# Revit family: HARMANN - REVIT - MAXEE - poziomy
name_source: partatom
category: Wyposażenie mechaniczne
units: mm (PartAtom-declared; Revit-internal decimal feet)

## family parameters
Klasyfikacja = Brak
Obiekt nadrzędny = Powierzchnia
Punkt obliczania pomieszczeń = Nie
Tnij formami wycięć po wczytaniu = Nie
Typ części = Normalny
Współdzielony = Nie
Wymiar okrągłego złącza = Użyj średnicy
Zachowaj orientację opisów = Nie

## types (40) — shared parameters
Autor = https://www.archispace.com
Domyślna rzędna = 1219.2 mm
Opis = Kanałowy wentylator bytowy
Producent = Harmann Polska Sp. z o.o.
Temperatura pracy T = 60 °C
Zasilanie Częstotliwość Minimalna fmin = 20 Hz
Zasilanie Częstotliwość Nominalna fnom = 50 Hz
Zasilanie Ilość faz = 3
Zasilanie napięcie nominalne Unom = 400 V

## per-type parameters (varying)
- MAXEE 1250/6/119600T: A=1370 mm; Akc ESD=HARMANN - Akcesoria - ESD : ESD 1250; Akc EXP=HARMANN - Akcesoria - EXP : EXP 1250; Akc FAL=HARMANN - Akcesoria - FAL : FAL 1250; Akc FSD=HARMANN - Akcesoria - FSD : FSD 11; Akc RAF=HARMANN - Akcesoria - RAF : RAF 1250; Akc RVK H=HARMANN - Akcesoria - RVK H : RVK H 1250; Akc RVS=HARMANN - Akcesoria - RVS : RVS 1250; Akc SGE=HARMANN - Akcesoria - SGE : SGE 1250; Akc SGE dla ESD=HARMANN - Akcesoria - SGE : SGE 1400; B=728 mm; C=1320 mm; Ciśnienie akustyczne nominalne obudowa Lpa=89 dB(A); D=1250 mm; D2=1256 mm; Długość MAXEE=728 mm; F=997 mm; Klasa odporności ogniowej Tmax=brak; Lookup Table Name=MAXEE; MAXEE=HARMANN - MAXEE : MAXEE 1250/6/119600T; Masa=550.00 kg; Moc akustyczna nominalna obudowa Lwa=96 dB(A); Model=MAXEE 1250/6/119600T; N1=40  [stored 0.131234 ft]; Numer artykułu=16259200; Obroty nominalne nnom=1190.000 obr./min; Powietrze Przepływ Maksymalny Qmax=119640.0 m³/h; Powietrze ciśnienie statyczne maksymalne dPmax=1015.0 Pa; R2=625 mm; Wysokość=498 mm; Wysokość FAL=270 mm; Wysokość FSD=94 mm; Zasilanie Częstotliwość Maksymalna fmax=60 Hz; Zasilanie Moc maksymalna Pmax=37683 W; Zasilanie natężenie maksymalne Imax=69 A
- MAXEE 1250/6/109300T: A=1370 mm; Akc ESD=HARMANN - Akcesoria - ESD : ESD 1250; Akc EXP=HARMANN - Akcesoria - EXP : EXP 1250; Akc FAL=HARMANN - Akcesoria - FAL : FAL 1250; Akc FSD=HARMANN - Akcesoria - FSD : FSD 11; Akc RAF=HARMANN - Akcesoria - RAF : RAF 1250; Akc RVK H=HARMANN - Akcesoria - RVK H : RVK H 1250; Akc RVS=HARMANN - Akcesoria - RVS : RVS 1250; Akc SGE=HARMANN - Akcesoria - SGE : SGE 1250; Akc SGE dla ESD=HARMANN - Akcesoria - SGE : SGE 1250; B=728 mm; C=1320 mm; Ciśnienie akustyczne nominalne obudowa Lpa=88 dB(A); D=1250 mm; D2=1256 mm; Długość MAXEE=728 mm; F=997 mm; Klasa odporności ogniowej Tmax=brak; Lookup Table Name=MAXEE; MAXEE=HARMANN - MAXEE : MAXEE 1250/6/109300T; Masa=376.00 kg; Moc akustyczna nominalna obudowa Lwa=95 dB(A); Model=MAXEE 1250/6/109300T; N1=39  [stored 0.127953 ft]; Numer artykułu=16258300; Obroty nominalne nnom=1080.000 obr./min; Powietrze Przepływ Maksymalny Qmax=109260.0 m³/h; Powietrze ciśnienie statyczne maksymalne dPmax=835.0 Pa; R2=625 mm; Wysokość=498 mm; Wysokość FAL=270 mm; Wysokość FSD=94 mm; Zasilanie Częstotliwość Maksymalna fmax=55 Hz; Zasilanie Moc maksymalna Pmax=28129 W; Zasilanie natężenie maksymalne Imax=52 A
- MAXEE 1250/6/98500T: A=1370 mm; Akc ESD=HARMANN - Akcesoria - ESD : ESD 1250; Akc EXP=HARMANN - Akcesoria - EXP : EXP 1250; Akc FAL=HARMANN - Akcesoria - FAL : FAL 1250; Akc FSD=HARMANN - Akcesoria - FSD : FSD 11; Akc RAF=HARMANN - Akcesoria - RAF : RAF 1250; Akc RVK H=HARMANN - Akcesoria - RVK H : RVK H 1250; Akc RVS=HARMANN - Akcesoria - RVS : RVS 1250; Akc SGE=HARMANN - Akcesoria - SGE : SGE 1250; Akc SGE dla ESD=HARMANN - Akcesoria - SGE : SGE 1400; B=728 mm; C=1320 mm; Ciśnienie akustyczne nominalne obudowa Lpa=89 dB(A); D=1250 mm; D2=1256 mm; Długość MAXEE=728 mm; F=997 mm; Klasa odporności ogniowej Tmax=brak; Lookup Table Name=MAXEE; MAXEE=HARMANN - MAXEE : MAXEE 1250/6/98500T; Masa=365.00 kg; Moc akustyczna nominalna obudowa Lwa=96 dB(A); Model=MAXEE 1250/6/98500T; N1=38  [stored 0.124672 ft]; Numer artykułu=16257900; Obroty nominalne nnom=990.000 obr./min; Powietrze Przepływ Maksymalny Qmax=98520.0 m³/h; Powietrze ciśnienie statyczne maksymalne dPmax=670.0 Pa; R2=625 mm; Wysokość=498 mm; Wysokość FAL=270 mm; Wysokość FSD=94 mm; Zasilanie Częstotliwość Maksymalna fmax=50 Hz; Zasilanie Moc maksymalna Pmax=21529 W; Zasilanie natężenie maksymalne Imax=41 A
- MAXEE 1250/6/79400T: A=1370 mm; Akc ESD=HARMANN - Akcesoria - ESD : ESD 1250; Akc EXP=HARMANN - Akcesoria - EXP : EXP 1250; Akc FAL=HARMANN - Akcesoria - FAL : FAL 1250; Akc FSD=HARMANN - Akcesoria - FSD : FSD 11; Akc RAF=HARMANN - Akcesoria - RAF : RAF 1250; Akc RVK H=HARMANN - Akcesoria - RVK H : RVK H 1250; Akc RVS=HARMANN - Akcesoria - RVS : RVS 1250; Akc SGE=HARMANN - Akcesoria - SGE : SGE 1250; Akc SGE dla ESD=HARMANN - Akcesoria - SGE : SGE 1400; B=728 mm; C=1320 mm; Ciśnienie akustyczne nominalne obudowa Lpa=80 dB(A); D=1250 mm; D2=1256 mm; Długość MAXEE=728 mm; F=874 mm; Klasa odporności ogniowej Tmax=400 [oC/2h]; Lookup Table Name=MAXEE; MAXEE=HARMANN - MAXEE : MAXEE 1250/6/79400T; Masa=280.00 kg; Moc akustyczna nominalna obudowa Lwa=87 dB(A); Model=MAXEE 1250/6/79400T; N1=37  [stored 0.121391 ft]; Numer artykułu=16257300; Obroty nominalne nnom=780.000 obr./min; Powietrze Przepływ Maksymalny Qmax=79450.0 m³/h; Powietrze ciśnienie statyczne maksymalne dPmax=420.0 Pa; R2=625 mm; Wysokość=498 mm; Wysokość FAL=270 mm; Wysokość FSD=94 mm; Zasilanie Częstotliwość Maksymalna fmax=40 Hz; Zasilanie Moc maksymalna Pmax=10850 W; Zasilanie natężenie maksymalne Imax=26 A
- MAXEE 1120/6/85800T: A=1240 mm; Akc ESD=HARMANN - Akcesoria - ESD : ESD 1120; Akc EXP=HARMANN - Akcesoria - EXP : EXP 1120; Akc FAL=HARMANN - Akcesoria - FAL : FAL 1120; Akc FSD=HARMANN - Akcesoria - FSD : FSD 11; Akc RAF=HARMANN - Akcesoria - RAF : RAF 1120; Akc RVK H=HARMANN - Akcesoria - RVK H : RVK H 1120; Akc RVS=HARMANN - Akcesoria - RVS : RVS 1120; Akc SGE=HARMANN - Akcesoria - SGE : SGE 1120; Akc SGE dla ESD=HARMANN - Akcesoria - SGE : SGE 1250; B=728 mm; C=1190 mm; Ciśnienie akustyczne nominalne obudowa Lpa=87 dB(A); D=1120 mm; D2=1126 mm; Długość MAXEE=728 mm; F=967 mm; Klasa odporności ogniowej Tmax=brak; Lookup Table Name=MAXEE; MAXEE=HARMANN - MAXEE : MAXEE 1120/6/85800T; Masa=345.00 kg; Moc akustyczna nominalna obudowa Lwa=94 dB(A); Model=MAXEE 1120/6/85800T; N1=36  [stored 0.11811 ft]; Numer artykułu=16271100; Obroty nominalne nnom=1190.000 obr./min; Powietrze Przepływ Maksymalny Qmax=85820.0 m³/h; Powietrze ciśnienie statyczne maksymalne dPmax=765.0 Pa; R2=560 mm; Wysokość=433 mm; Wysokość FAL=270 mm; Wysokość FSD=94 mm; Zasilanie Częstotliwość Maksymalna fmax=60 Hz; Zasilanie Moc maksymalna Pmax=20147 W; Zasilanie natężenie maksymalne Imax=38 A
- MAXEE 1120/6/71400T: A=1240 mm; Akc ESD=HARMANN - Akcesoria - ESD : ESD 1120; Akc EXP=HARMANN - Akcesoria - EXP : EXP 1120; Akc FAL=HARMANN - Akcesoria - FAL : FAL 1120; Akc FSD=HARMANN - Akcesoria - FSD : FSD 11; Akc RAF=HARMANN - Akcesoria - RAF : RAF 1120; Akc RVK H=HARMANN - Akcesoria - RVK H : RVK H 1120; Akc RVS=HARMANN - Akcesoria - RVS : RVS 1120; Akc SGE=HARMANN - Akcesoria - SGE : SGE 1120; Akc SGE dla ESD=HARMANN - Akcesoria - SGE : SGE 1250; B=728 mm; C=1190 mm; Ciśnienie akustyczne nominalne obudowa Lpa=86 dB(A); D=1120 mm; D2=1126 mm; Długość MAXEE=728 mm; F=844 mm; Klasa odporności ogniowej Tmax=brak; Lookup Table Name=MAXEE; MAXEE=HARMANN - MAXEE : MAXEE 1120/6/71400T; Masa=298.00 kg; Moc akustyczna nominalna obudowa Lwa=93 dB(A); Model=MAXEE 1120/6/71400T; N1=35  [stored 0.114829 ft]; Numer artykułu=16270700; Obroty nominalne nnom=990.000 obr./min; Powietrze Przepływ Maksymalny Qmax=71380.0 m³/h; Powietrze ciśnienie statyczne maksymalne dPmax=545.0 Pa; R2=560 mm; Wysokość=433 mm; Wysokość FAL=270 mm; Wysokość FSD=94 mm; Zasilanie Częstotliwość Maksymalna fmax=50 Hz; Zasilanie Moc maksymalna Pmax=12903 W; Zasilanie natężenie maksymalne Imax=24 A
- MAXEE 1120/6/62200T: A=1240 mm; Akc ESD=HARMANN - Akcesoria - ESD : ESD 1120; Akc EXP=HARMANN - Akcesoria - EXP : EXP 1120; Akc FAL=HARMANN - Akcesoria - FAL : FAL 1120; Akc FSD=HARMANN - Akcesoria - FSD : FSD 11; Akc RAF=HARMANN - Akcesoria - RAF : RAF 1120; Akc RVK H=HARMANN - Akcesoria - RVK H : RVK H 1120; Akc RVS=HARMANN - Akcesoria - RVS : RVS 1120; Akc SGE=HARMANN - Akcesoria - SGE : SGE 1120; Akc SGE dla ESD=HARMANN - Akcesoria - SGE : SGE 1250; B=728 mm; C=1190 mm; Ciśnienie akustyczne nominalne obudowa Lpa=80 dB(A); D=1120 mm; D2=1126 mm; Długość MAXEE=728 mm; F=745 mm; Klasa odporności ogniowej Tmax=brak; Lookup Table Name=MAXEE; MAXEE=HARMANN - MAXEE : MAXEE 1120/6/62200T; Masa=218.00 kg; Moc akustyczna nominalna obudowa Lwa=87 dB(A); Model=MAXEE 1120/6/62200T; N1=34  [stored 0.111549 ft]; Numer artykułu=16271500; Obroty nominalne nnom=860.000 obr./min; Powietrze Przepływ Maksymalny Qmax=62250.0 m³/h; Powietrze ciśnienie statyczne maksymalne dPmax=390.0 Pa; R2=560 mm; Wysokość=433 mm; Wysokość FAL=270 mm; Wysokość FSD=94 mm; Zasilanie Częstotliwość Maksymalna fmax=45 Hz; Zasilanie Moc maksymalna Pmax=7053 W; Zasilanie natężenie maksymalne Imax=16 A
- MAXEE 1000/4/76100T: A=1110 mm; Akc ESD=HARMANN - Akcesoria - ESD : ESD 1000; Akc EXP=HARMANN - Akcesoria - EXP : EXP 1000; Akc FAL=HARMANN - Akcesoria - FAL : FAL 1000; Akc FSD=HARMANN - Akcesoria - FSD : FSD 11; Akc RAF=HARMANN - Akcesoria - RAF : RAF 1000; Akc RVK H=HARMANN - Akcesoria - RVK H : RVK H 1000; Akc RVS=HARMANN - Akcesoria - RVS : RVS 1000; Akc SGE=HARMANN - Akcesoria - SGE : SGE 1000; Akc SGE dla ESD=HARMANN - Akcesoria - SGE : SGE 1120; B=638 mm; C=1070 mm; Ciśnienie akustyczne nominalne obudowa Lpa=87 dB(A); D=1000 mm; D2=1006 mm; Długość MAXEE=638 mm; F=834 mm; Klasa odporności ogniowej Tmax=brak; Lookup Table Name=MAXEE; MAXEE=HARMANN - MAXEE : MAXEE 1000/4/76100T; Masa=280.00 kg; Moc akustyczna nominalna obudowa Lwa=94 dB(A); Model=MAXEE 1000/4/76100T; N1=33  [stored 0.108268 ft]; Numer artykułu=16264100; Obroty nominalne nnom=1480.000 obr./min; Powietrze Przepływ Maksymalny Qmax=76095.0 m³/h; Powietrze ciśnienie statyczne maksymalne dPmax=970.0 Pa; R2=500 mm; Wysokość=383 mm; Wysokość FAL=250 mm; Wysokość FSD=94 mm; Zasilanie Częstotliwość Maksymalna fmax=50 Hz; Zasilanie Moc maksymalna Pmax=23206 W; Zasilanie natężenie maksymalne Imax=41 A
- MAXEE 1000/4/75800T: A=1110 mm; Akc ESD=HARMANN - Akcesoria - ESD : ESD 1000; Akc EXP=HARMANN - Akcesoria - EXP : EXP 1000; Akc FAL=HARMANN - Akcesoria - FAL : FAL 1000; Akc FSD=HARMANN - Akcesoria - FSD : FSD 11; Akc RAF=HARMANN - Akcesoria - RAF : RAF 1000; Akc RVK H=HARMANN - Akcesoria - RVK H : RVK H 1000; Akc RVS=HARMANN - Akcesoria - RVS : RVS 1000; Akc SGE=HARMANN - Akcesoria - SGE : SGE 1000; Akc SGE dla ESD=HARMANN - Akcesoria - SGE : SGE 1120; B=638 mm; C=1070 mm; Ciśnienie akustyczne nominalne obudowa Lpa=84 dB(A); D=1000 mm; D2=1006 mm; Długość MAXEE=638 mm; F=872 mm; Klasa odporności ogniowej Tmax=brak; Lookup Table Name=MAXEE_HT; MAXEE=HARMANN - MAXEE : MAXEE 1000/4/75800T; Masa=313.00 kg; Moc akustyczna nominalna obudowa Lwa=91 dB(A); Model=MAXEE 1000/4/75800T; N1=32  [stored 0.104987 ft]; Numer artykułu=16264800; Obroty nominalne nnom=1480.000 obr./min; Powietrze Przepływ Maksymalny Qmax=75810.0 m³/h; Powietrze ciśnienie statyczne maksymalne dPmax=980.0 Pa; R2=500 mm; Wysokość=383 mm; Wysokość FAL=250 mm; Wysokość FSD=94 mm; Zasilanie Częstotliwość Maksymalna fmax=50 Hz; Zasilanie Moc maksymalna Pmax=22034 W; Zasilanie natężenie maksymalne Imax=41 A
- MAXEE 1000/4/67500T: A=1110 mm; Akc ESD=HARMANN - Akcesoria - ESD : ESD 1000; Akc EXP=HARMANN - Akcesoria - EXP : EXP 1000; Akc FAL=HARMANN - Akcesoria - FAL : FAL 1000; Akc FSD=HARMANN - Akcesoria - FSD : FSD 11; Akc RAF=HARMANN - Akcesoria - RAF : RAF 1000; Akc RVK H=HARMANN - Akcesoria - RVK H : RVK H 1000; Akc RVS=HARMANN - Akcesoria - RVS : RVS 1000; Akc SGE=HARMANN - Akcesoria - SGE : SGE 1000; Akc SGE dla ESD=HARMANN - Akcesoria - SGE : SGE 1120; B=638 mm; C=1070 mm; Ciśnienie akustyczne nominalne obudowa Lpa=82 dB(A); D=1000 mm; D2=1006 mm; Długość MAXEE=638 mm; F=814 mm; Klasa odporności ogniowej Tmax=brak; Lookup Table Name=MAXEE; MAXEE=HARMANN - MAXEE : MAXEE 1000/4/67500T; Masa=264.00 kg; Moc akustyczna nominalna obudowa Lwa=89 dB(A); Model=MAXEE 1000/4/67500T; N1=31  [stored 0.101706 ft]; Numer artykułu=16263600; Obroty nominalne nnom=1330.000 obr./min; Powietrze Przepływ Maksymalny Qmax=67550.0 m³/h; Powietrze ciśnienie statyczne maksymalne dPmax=1160.0 Pa; R2=500 mm; Wysokość=383 mm; Wysokość FAL=250 mm; Wysokość FSD=94 mm; Zasilanie Częstotliwość Maksymalna fmax=45 Hz; Zasilanie Moc maksymalna Pmax=16042 W; Zasilanie natężenie maksymalne Imax=33 A
- MAXEE 1000/6/60100T: A=1110 mm; Akc ESD=HARMANN - Akcesoria - ESD : ESD 1000; Akc EXP=HARMANN - Akcesoria - EXP : EXP 1000; Akc FAL=HARMANN - Akcesoria - FAL : FAL 1000; Akc FSD=HARMANN - Akcesoria - FSD : FSD 11; Akc RAF=HARMANN - Akcesoria - RAF : RAF 1000; Akc RVK H=HARMANN - Akcesoria - RVK H : RVK H 1000; Akc RVS=HARMANN - Akcesoria - RVS : RVS 1000; Akc SGE=HARMANN - Akcesoria - SGE : SGE 1000; Akc SGE dla ESD=HARMANN - Akcesoria - SGE : SGE 1120; B=638 mm; C=1070 mm; Ciśnienie akustyczne nominalne obudowa Lpa=78 dB(A); D=1000 mm; D2=1006 mm; Długość MAXEE=638 mm; F=814 mm; Klasa odporności ogniowej Tmax=brak; Lookup Table Name=MAXEE; MAXEE=HARMANN - MAXEE : MAXEE 1000/6/60100T; Masa=265.00 kg; Moc akustyczna nominalna obudowa Lwa=85 dB(A); Model=MAXEE 1000/6/60100T; N1=30  [stored 0.0984252 ft]; Numer artykułu=16263100; Obroty nominalne nnom=1185.000 obr./min; Powietrze Przepływ Maksymalny Qmax=60140.0 m³/h; Powietrze ciśnienie statyczne maksymalne dPmax=610.0 Pa; R2=500 mm; Wysokość=383 mm; Wysokość FAL=250 mm; Wysokość FSD=94 mm; Zasilanie Częstotliwość Maksymalna fmax=60 Hz; Zasilanie Moc maksymalna Pmax=15647 W; Zasilanie natężenie maksymalne Imax=22 A
- MAXEE 1000/4/60000T: A=1110 mm; Akc ESD=HARMANN - Akcesoria - ESD : ESD 1000; Akc EXP=HARMANN - Akcesoria - EXP : EXP 1000; Akc FAL=HARMANN - Akcesoria - FAL : FAL 1000; Akc FSD=HARMANN - Akcesoria - FSD : FSD 11; Akc RAF=HARMANN - Akcesoria - RAF : RAF 1000; Akc RVK H=HARMANN - Akcesoria - RVK H : RVK H 1000; Akc RVS=HARMANN - Akcesoria - RVS : RVS 1000; Akc SGE=HARMANN - Akcesoria - SGE : SGE 1000; Akc SGE dla ESD=HARMANN - Akcesoria - SGE : SGE 1120; B=638 mm; C=1070 mm; Ciśnienie akustyczne nominalne obudowa Lpa=78 dB(A); D=1000 mm; D2=1006 mm; Długość MAXEE=638 mm; F=770 mm; Klasa odporności ogniowej Tmax=brak; Lookup Table Name=MAXEE; MAXEE=HARMANN - MAXEE : MAXEE 1000/4/60000T; Masa=220.00 kg; Moc akustyczna nominalna obudowa Lwa=85 dB(A); Model=MAXEE 1000/4/60000T; N1=29  [stored 0.0951444 ft]; Numer artykułu=16261800; Obroty nominalne nnom=1185.000 obr./min; Powietrze Przepływ Maksymalny Qmax=60040.0 m³/h; Powietrze ciśnienie statyczne maksymalne dPmax=600.0 Pa; R2=500 mm; Wysokość=383 mm; Wysokość FAL=250 mm; Wysokość FSD=94 mm; Zasilanie Częstotliwość Maksymalna fmax=40 Hz; Zasilanie Moc maksymalna Pmax=11300 W; Zasilanie natężenie maksymalne Imax=27 A
- MAXEE 1000/6/49300T: A=1110 mm; Akc ESD=HARMANN - Akcesoria - ESD : ESD 1000; Akc EXP=HARMANN - Akcesoria - EXP : EXP 1000; Akc FAL=HARMANN - Akcesoria - FAL : FAL 1000; Akc FSD=HARMANN - Akcesoria - FSD : FSD 11; Akc RAF=HARMANN - Akcesoria - RAF : RAF 1000; Akc RVK H=HARMANN - Akcesoria - RVK H : RVK H 1000; Akc RVS=HARMANN - Akcesoria - RVS : RVS 1000; Akc SGE=HARMANN - Akcesoria - SGE : SGE 1000; Akc SGE dla ESD=HARMANN - Akcesoria - SGE : SGE 1120; B=638 mm; C=1070 mm; Ciśnienie akustyczne nominalne obudowa Lpa=78 dB(A); D=1000 mm; D2=1006 mm; Długość MAXEE=638 mm; F=715 mm; Klasa odporności ogniowej Tmax=brak; Lookup Table Name=MAXEE_HT; MAXEE=HARMANN - MAXEE : MAXEE 1000/6/49300T; Masa=195.00 kg; Moc akustyczna nominalna obudowa Lwa=85 dB(A); Model=MAXEE 1000/6/49300T; N1=28  [stored 0.0918635 ft]; Numer artykułu=16265200; Obroty nominalne nnom=980.000 obr./min; Powietrze Przepływ Maksymalny Qmax=49290.0 m³/h; Powietrze ciśnienie statyczne maksymalne dPmax=400.0 Pa; R2=500 mm; Wysokość=383 mm; Wysokość FAL=250 mm; Wysokość FSD=94 mm; Zasilanie Częstotliwość Maksymalna fmax=50 Hz; Zasilanie Moc maksymalna Pmax=6663 W; Zasilanie natężenie maksymalne Imax=14 A
- MAXEE 900/4/60300T: A=1010 mm; Akc ESD=HARMANN - Akcesoria - ESD : ESD 900; Akc EXP=HARMANN - Akcesoria - EXP : EXP 900; Akc FAL=HARMANN - Akcesoria - FAL : FAL 900; Akc FSD=HARMANN - Akcesoria - FSD : FSD 10; Akc RAF=HARMANN - Akcesoria - RAF : RAF 900; Akc RVK H=HARMANN - Akcesoria - RVK H : RVK H 900; Akc RVS=HARMANN - Akcesoria - RVS : RVS 900; Akc SGE=HARMANN - Akcesoria - SGE : SGE 900; Akc SGE dla ESD=HARMANN - Akcesoria - SGE : SGE 1000; B=638 mm; C=970 mm; Ciśnienie akustyczne nominalne obudowa Lpa=83 dB(A); D=900 mm; D2=906 mm; Długość MAXEE=638 mm; F=794 mm; Klasa odporności ogniowej Tmax=brak; Lookup Table Name=MAXEE; MAXEE=HARMANN - MAXEE : MAXEE 900/4/60300T; Masa=244.80 kg; Moc akustyczna nominalna obudowa Lwa=90 dB(A); Model=MAXEE 900/4/60300T; N1=27  [stored 0.0885827 ft]; Numer artykułu=16268300; Obroty nominalne nnom=1630.000 obr./min; Powietrze Przepływ Maksymalny Qmax=60290.0 m³/h; Powietrze ciśnienie statyczne maksymalne dPmax=920.0 Pa; R2=450 mm; Wysokość=373 mm; Wysokość FAL=170 mm; Wysokość FSD=94 mm; Zasilanie Częstotliwość Maksymalna fmax=55 Hz; Zasilanie Moc maksymalna Pmax=17319 W; Zasilanie natężenie maksymalne Imax=31 A
- MAXEE 900/4/54700T: A=1010 mm; Akc ESD=HARMANN - Akcesoria - ESD : ESD 900; Akc EXP=HARMANN - Akcesoria - EXP : EXP 900; Akc FAL=HARMANN - Akcesoria - FAL : FAL 900; Akc FSD=HARMANN - Akcesoria - FSD : FSD 10; Akc RAF=HARMANN - Akcesoria - RAF : RAF 900; Akc RVK H=HARMANN - Akcesoria - RVK H : RVK H 900; Akc RVS=HARMANN - Akcesoria - RVS : RVS 900; Akc SGE=HARMANN - Akcesoria - SGE : SGE 900; Akc SGE dla ESD=HARMANN - Akcesoria - SGE : SGE 1000; B=638 mm; C=970 mm; Ciśnienie akustyczne nominalne obudowa Lpa=83 dB(A); D=900 mm; D2=906 mm; Długość MAXEE=638 mm; F=750 mm; Klasa odporności ogniowej Tmax=brak; Lookup Table Name=MAXEE; MAXEE=HARMANN - MAXEE : MAXEE 900/4/54700T; Masa=200.80 kg; Moc akustyczna nominalna obudowa Lwa=90 dB(A); Model=MAXEE 900/4/54700T; N1=26  [stored 0.0853018 ft]; Numer artykułu=16268300; Obroty nominalne nnom=1480.000 obr./min; Powietrze Przepływ Maksymalny Qmax=54730.0 m³/h; Powietrze ciśnienie statyczne maksymalne dPmax=760.0 Pa; R2=450 mm; Wysokość=373 mm; Wysokość FAL=170 mm; Wysokość FSD=94 mm; Zasilanie Częstotliwość Maksymalna fmax=50 Hz; Zasilanie Moc maksymalna Pmax=13233 W; Zasilanie natężenie maksymalne Imax=25 A
- MAXEE 900/4/49400T: A=1010 mm; Akc ESD=HARMANN - Akcesoria - ESD : ESD 900; Akc EXP=HARMANN - Akcesoria - EXP : EXP 900; Akc FAL=HARMANN - Akcesoria - FAL : FAL 900; Akc FSD=HARMANN - Akcesoria - FSD : FSD 10; Akc RAF=HARMANN - Akcesoria - RAF : RAF 900; Akc RVK H=HARMANN - Akcesoria - RVK H : RVK H 900; Akc RVS=HARMANN - Akcesoria - RVS : RVS 900; Akc SGE=HARMANN - Akcesoria - SGE : SGE 900; Akc SGE dla ESD=HARMANN - Akcesoria - SGE : SGE 1000; B=638 mm; C=970 mm; Ciśnienie akustyczne nominalne obudowa Lpa=80 dB(A); D=900 mm; D2=906 mm; Długość MAXEE=638 mm; F=670 mm; Klasa odporności ogniowej Tmax=brak; Lookup Table Name=MAXEE; MAXEE=HARMANN - MAXEE : MAXEE 900/4/49400T; Masa=169.20 kg; Moc akustyczna nominalna obudowa Lwa=87 dB(A); Model=MAXEE 900/4/49400T; N1=25  [stored 0.082021 ft]; Numer artykułu=16270200; Obroty nominalne nnom=1320.000 obr./min; Powietrze Przepływ Maksymalny Qmax=49370.0 m³/h; Powietrze ciśnienie statyczne maksymalne dPmax=580.0 Pa; R2=450 mm; Wysokość=373 mm; Wysokość FAL=170 mm; Wysokość FSD=94 mm; Zasilanie Częstotliwość Maksymalna fmax=45 Hz; Zasilanie Moc maksymalna Pmax=9518 W; Zasilanie natężenie maksymalne Imax=18 A
- MAXEE 900/6/43400T: A=1010 mm; Akc ESD=HARMANN - Akcesoria - ESD : ESD 900; Akc EXP=HARMANN - Akcesoria - EXP : EXP 900; Akc FAL=HARMANN - Akcesoria - FAL : FAL 900; Akc FSD=HARMANN - Akcesoria - FSD : FSD 10; Akc RAF=HARMANN - Akcesoria - RAF : RAF 900; Akc RVK H=HARMANN - Akcesoria - RVK H : RVK H 900; Akc RVS=HARMANN - Akcesoria - RVS : RVS 900; Akc SGE=HARMANN - Akcesoria - SGE : SGE 900; Akc SGE dla ESD=HARMANN - Akcesoria - SGE : SGE 1000; B=638 mm; C=970 mm; Ciśnienie akustyczne nominalne obudowa Lpa=76 dB(A); D=900 mm; D2=906 mm; Długość MAXEE=638 mm; F=695 mm; Klasa odporności ogniowej Tmax=brak; Lookup Table Name=MAXEE; MAXEE=HARMANN - MAXEE : MAXEE 900/6/43400T; Masa=177.20 kg; Moc akustyczna nominalna obudowa Lwa=83 dB(A); Model=MAXEE 900/6/43400T; N1=24  [stored 0.0787402 ft]; Numer artykułu=16269500; Obroty nominalne nnom=1170.000 obr./min; Powietrze Przepływ Maksymalny Qmax=43390.0 m³/h; Powietrze ciśnienie statyczne maksymalne dPmax=990.0 Pa; R2=450 mm; Wysokość=373 mm; Wysokość FAL=170 mm; Wysokość FSD=94 mm; Zasilanie Częstotliwość Maksymalna fmax=60 Hz; Zasilanie Moc maksymalna Pmax=6601 W; Zasilanie natężenie maksymalne Imax=13 A
- MAXEE 900/4/43300T: A=1010 mm; Akc ESD=HARMANN - Akcesoria - ESD : ESD 900; Akc EXP=HARMANN - Akcesoria - EXP : EXP 900; Akc FAL=HARMANN - Akcesoria - FAL : FAL 900; Akc FSD=HARMANN - Akcesoria - FSD : FSD 10; Akc RAF=HARMANN - Akcesoria - RAF : RAF 900; Akc RVK H=HARMANN - Akcesoria - RVK H : RVK H 900; Akc RVS=HARMANN - Akcesoria - RVS : RVS 900; Akc SGE=HARMANN - Akcesoria - SGE : SGE 900; Akc SGE dla ESD=HARMANN - Akcesoria - SGE : SGE 1000; B=638 mm; C=970 mm; Ciśnienie akustyczne nominalne obudowa Lpa=77 dB(A); D=900 mm; D2=906 mm; Długość MAXEE=638 mm; F=725 mm; Klasa odporności ogniowej Tmax=brak; Lookup Table Name=MAXEE; MAXEE=HARMANN - MAXEE : MAXEE 900/4/43300T; Masa=158.20 kg; Moc akustyczna nominalna obudowa Lwa=84 dB(A); Model=MAXEE 900/4/43300T; N1=23  [stored 0.0754593 ft]; Numer artykułu=1628800; Obroty nominalne nnom=1170.000 obr./min; Powietrze Przepływ Maksymalny Qmax=43340.0 m³/h; Powietrze ciśnienie statyczne maksymalne dPmax=440.0 Pa; R2=450 mm; Wysokość=373 mm; Wysokość FAL=170 mm; Wysokość FSD=94 mm; Zasilanie Częstotliwość Maksymalna fmax=40 Hz; Zasilanie Moc maksymalna Pmax=6500 W; Zasilanie natężenie maksymalne Imax=15 A
- MAXEE 800/4/48700T: A=900 mm; Akc ESD=HARMANN - Akcesoria - ESD : ESD 800; Akc EXP=HARMANN - Akcesoria - EXP : EXP 800; Akc FAL=HARMANN - Akcesoria - FAL : FAL 800; Akc FSD=HARMANN - Akcesoria - FSD : FSD 10; Akc RAF=HARMANN - Akcesoria - RAF : RAF 800; Akc RVK H=HARMANN - Akcesoria - RVK H : RVK H 800; Akc RVS=HARMANN - Akcesoria - RVS : RVS 800; Akc SGE=HARMANN - Akcesoria - SGE : SGE 800; Akc SGE dla ESD=HARMANN - Akcesoria - SGE : SGE 900; B=648 mm; C=860 mm; Ciśnienie akustyczne nominalne obudowa Lpa=82 dB(A); D=800 mm; D2=806 mm; Długość MAXEE=648 mm; F=725 mm; Klasa odporności ogniowej Tmax=brak; Lookup Table Name=MAXEE; MAXEE=HARMANN - MAXEE : MAXEE 800/4/48700T; Masa=186.10 kg; Moc akustyczna nominalna obudowa Lwa=89 dB(A); Model=MAXEE 800/4/48700T; N1=22  [stored 0.0721785 ft]; Numer artykułu=16246300; Obroty nominalne nnom=1780.000 obr./min; Powietrze Przepływ Maksymalny Qmax=48730.0 m³/h; Powietrze ciśnienie statyczne maksymalne dPmax=900.0 Pa; R2=400 mm; Wysokość=328 mm; Wysokość FAL=160 mm; Wysokość FSD=94 mm; Zasilanie Częstotliwość Maksymalna fmax=60 Hz; Zasilanie Moc maksymalna Pmax=9704 W; Zasilanie natężenie maksymalne Imax=24 A
- MAXEE 800/4/39900T: A=900 mm; Akc ESD=HARMANN - Akcesoria - ESD : ESD 800; Akc EXP=HARMANN - Akcesoria - EXP : EXP 800; Akc FAL=HARMANN - Akcesoria - FAL : FAL 800; Akc FSD=HARMANN - Akcesoria - FSD : FSD 10; Akc RAF=HARMANN - Akcesoria - RAF : RAF 800; Akc RVK H=HARMANN - Akcesoria - RVK H : RVK H 800; Akc RVS=HARMANN - Akcesoria - RVS : RVS 800; Akc SGE=HARMANN - Akcesoria - SGE : SGE 800; Akc SGE dla ESD=HARMANN - Akcesoria - SGE : SGE 900; B=648 mm; C=860 mm; Ciśnienie akustyczne nominalne obudowa Lpa=81 dB(A); D=800 mm; D2=806 mm; Długość MAXEE=648 mm; F=670 mm; Klasa odporności ogniowej Tmax=brak; Lookup Table Name=MAXEE; MAXEE=HARMANN - MAXEE : MAXEE 800/4/39900T; Masa=153.10 kg; Moc akustyczna nominalna obudowa Lwa=88 dB(A); Model=MAXEE 800/4/39900T; N1=21  [stored 0.0688976 ft]; Numer artykułu=16256400; Obroty nominalne nnom=1480.000 obr./min; Powietrze Przepływ Maksymalny Qmax=39890.0 m³/h; Powietrze ciśnienie statyczne maksymalne dPmax=650.0 Pa; R2=400 mm; Wysokość=328 mm; Wysokość FAL=160 mm; Wysokość FSD=94 mm; Zasilanie Częstotliwość Maksymalna fmax=50 Hz; Zasilanie Moc maksymalna Pmax=7656 W; Zasilanie natężenie maksymalne Imax=15 A
- MAXEE 800/6/36800T: A=900 mm; Akc ESD=HARMANN - Akcesoria - ESD : ESD 800; Akc EXP=HARMANN - Akcesoria - EXP : EXP 800; Akc FAL=HARMANN - Akcesoria - FAL : FAL 800; Akc FSD=HARMANN - Akcesoria - FSD : FSD 10; Akc RAF=HARMANN - Akcesoria - RAF : RAF 800; Akc RVK H=HARMANN - Akcesoria - RVK H : RVK H 800; Akc RVS=HARMANN - Akcesoria - RVS : RVS 800; Akc SGE=HARMANN - Akcesoria - SGE : SGE 800; Akc SGE dla ESD=HARMANN - Akcesoria - SGE : SGE 900; B=648 mm; C=860 mm; Ciśnienie akustyczne nominalne obudowa Lpa=78 dB(A); D=800 mm; D2=806 mm; Długość MAXEE=648 mm; F=670 mm; Klasa odporności ogniowej Tmax=brak; Lookup Table Name=MAXEE; MAXEE=HARMANN - MAXEE : MAXEE 800/6/36800T; Masa=161.10 kg; Moc akustyczna nominalna obudowa Lwa=85 dB(A); Model=MAXEE 800/6/36800T; N1=20  [stored 0.0656168 ft]; Numer artykułu=16254300; Obroty nominalne nnom=1370.000 obr./min; Powietrze Przepływ Maksymalny Qmax=36860.0 m³/h; Powietrze ciśnienie statyczne maksymalne dPmax=530.0 Pa; R2=400 mm; Wysokość=328 mm; Wysokość FAL=160 mm; Wysokość FSD=94 mm; Zasilanie Częstotliwość Maksymalna fmax=70 Hz; Zasilanie Moc maksymalna Pmax=6296 W; Zasilanie natężenie maksymalne Imax=12 A
- MAXEE 800/4/31600T: A=900 mm; Akc ESD=HARMANN - Akcesoria - ESD : ESD 800; Akc EXP=HARMANN - Akcesoria - EXP : EXP 800; Akc FAL=HARMANN - Akcesoria - FAL : FAL 800; Akc FSD=HARMANN - Akcesoria - FSD : FSD 10; Akc RAF=HARMANN - Akcesoria - RAF : RAF 800; Akc RVK H=HARMANN - Akcesoria - RVK H : RVK H 800; Akc RVS=HARMANN - Akcesoria - RVS : RVS 800; Akc SGE=HARMANN - Akcesoria - SGE : SGE 800; Akc SGE dla ESD=HARMANN - Akcesoria - SGE : SGE 900; B=648 mm; C=860 mm; Ciśnienie akustyczne nominalne obudowa Lpa=74 dB(A); D=800 mm; D2=806 mm; Długość MAXEE=648 mm; F=516 mm; Klasa odporności ogniowej Tmax=brak; Lookup Table Name=MAXEE; MAXEE=HARMANN - MAXEE : MAXEE 800/4/31600T; Masa=142.10 kg; Moc akustyczna nominalna obudowa Lwa=81 dB(A); Model=MAXEE 800/4/31600T; N1=19  [stored 0.062336 ft]; Numer artykułu=16253000; Obroty nominalne nnom=1180.000 obr./min; Powietrze Przepływ Maksymalny Qmax=31640.0 m³/h; Powietrze ciśnienie statyczne maksymalne dPmax=780.0 Pa; R2=400 mm; Wysokość=328 mm; Wysokość FAL=160 mm; Wysokość FSD=94 mm; Zasilanie Częstotliwość Maksymalna fmax=40 Hz; Zasilanie Moc maksymalna Pmax=4780 W; Zasilanie natężenie maksymalne Imax=10 A
- MAXEE 800/4/30800T: A=900 mm; Akc ESD=HARMANN - Akcesoria - ESD : ESD 800; Akc EXP=HARMANN - Akcesoria - EXP : EXP 800; Akc FAL=HARMANN - Akcesoria - FAL : FAL 800; Akc FSD=HARMANN - Akcesoria - FSD : FSD 10; Akc RAF=HARMANN - Akcesoria - RAF : RAF 800; Akc RVK H=HARMANN - Akcesoria - RVK H : RVK H 800; Akc RVS=HARMANN - Akcesoria - RVS : RVS 800; Akc SGE=HARMANN - Akcesoria - SGE : SGE 800; Akc SGE dla ESD=HARMANN - Akcesoria - SGE : SGE 900; B=648 mm; C=860 mm; Ciśnienie akustyczne nominalne obudowa Lpa=74 dB(A); D=800 mm; D2=806 mm; Długość MAXEE=648 mm; F=516 mm; Klasa odporności ogniowej Tmax=brak; Lookup Table Name=MAXEE; MAXEE=HARMANN - MAXEE : MAXEE 800/4/30800T; Masa=117.10 kg; Moc akustyczna nominalna obudowa Lwa=81 dB(A); Model=MAXEE 800/4/30800T; N1=18  [stored 0.0590551 ft]; Numer artykułu=16252000; Obroty nominalne nnom=1150.000 obr./min; Powietrze Przepływ Maksymalny Qmax=30800.0 m³/h; Powietrze ciśnienie statyczne maksymalne dPmax=380.0 Pa; R2=400 mm; Wysokość=328 mm; Wysokość FAL=160 mm; Wysokość FSD=94 mm; Zasilanie Częstotliwość Maksymalna fmax=40 Hz; Zasilanie Moc maksymalna Pmax=3816 W; Zasilanie natężenie maksymalne Imax=10 A
- MAXEE 800/6/26500T: A=900 mm; Akc ESD=HARMANN - Akcesoria - ESD : ESD 800; Akc EXP=HARMANN - Akcesoria - EXP : EXP 800; Akc FAL=HARMANN - Akcesoria - FAL : FAL 800; Akc FSD=HARMANN - Akcesoria - FSD : FSD 10; Akc RAF=HARMANN - Akcesoria - RAF : RAF 800; Akc RVK H=HARMANN - Akcesoria - RVK H : RVK H 800; Akc RVS=HARMANN - Akcesoria - RVS : RVS 800; Akc SGE=HARMANN - Akcesoria - SGE : SGE 800; Akc SGE dla ESD=HARMANN - Akcesoria - SGE : SGE 900; B=648 mm; C=860 mm; Ciśnienie akustyczne nominalne obudowa Lpa=73 dB(A); D=800 mm; D2=806 mm; Długość MAXEE=648 mm; F=516 mm; Klasa odporności ogniowej Tmax=brak; Lookup Table Name=MAXEE; MAXEE=HARMANN - MAXEE : MAXEE 800/6/26500T; Masa=114.10 kg; Moc akustyczna nominalna obudowa Lwa=80 dB(A); Model=MAXEE 800/6/26500T; N1=17  [stored 0.0557743 ft]; Numer artykułu=16250100; Obroty nominalne nnom=980.000 obr./min; Powietrze Przepływ Maksymalny Qmax=26520.0 m³/h; Powietrze ciśnienie statyczne maksymalne dPmax=280.0 Pa; R2=400 mm; Wysokość=328 mm; Wysokość FAL=160 mm; Wysokość FSD=94 mm; Zasilanie Częstotliwość Maksymalna fmax=50 Hz; Zasilanie Moc maksymalna Pmax=3298 W; Zasilanie natężenie maksymalne Imax=5 A
- MAXEE 710/4/36500T: A=810 mm; Akc ESD=HARMANN - Akcesoria - ESD : ESD 710; Akc EXP=HARMANN - Akcesoria - EXP : EXP 710; Akc FAL=HARMANN - Akcesoria - FAL : FAL 710; Akc FSD=HARMANN - Akcesoria - FSD : FSD 04; Akc RAF=HARMANN - Akcesoria - RAF : RAF 710; Akc RVK H=HARMANN - Akcesoria - RVK H : RVK H 710; Akc RVS=HARMANN - Akcesoria - RVS : RVS 710; Akc SGE=HARMANN - Akcesoria - SGE : SGE 710; Akc SGE dla ESD=HARMANN - Akcesoria - SGE : SGE 800; B=433 mm; C=770 mm; Ciśnienie akustyczne nominalne obudowa Lpa=77 dB(A); D=710 mm; D2=716 mm; Długość MAXEE=433 mm; F=516 mm; Klasa odporności ogniowej Tmax=brak; Lookup Table Name=MAXEE; MAXEE=HARMANN - MAXEE : MAXEE 710/4/36500T; Masa=98.50 kg; Moc akustyczna nominalna obudowa Lwa=84 dB(A); Model=MAXEE 710/4/36500T; N1=16  [stored 0.0524934 ft]; Numer artykułu=15414100; Obroty nominalne nnom=1920.000 obr./min; Powietrze Przepływ Maksymalny Qmax=33665.0 m³/h; Powietrze ciśnienie statyczne maksymalne dPmax=715.0 Pa; R2=355 mm; Wysokość=303.5 mm; Wysokość FAL=119 mm; Wysokość FSD=57 mm; Zasilanie Częstotliwość Maksymalna fmax=60 Hz; Zasilanie Moc maksymalna Pmax=8500 W; Zasilanie natężenie maksymalne Imax=14 A
- MAXEE 710/6/22500T: A=810 mm; Akc ESD=HARMANN - Akcesoria - ESD : ESD 710; Akc EXP=HARMANN - Akcesoria - EXP : EXP 710; Akc FAL=HARMANN - Akcesoria - FAL : FAL 710; Akc FSD=HARMANN - Akcesoria - FSD : FSD 04; Akc RAF=HARMANN - Akcesoria - RAF : RAF 710; Akc RVK H=HARMANN - Akcesoria - RVK H : RVK H 710; Akc RVS=HARMANN - Akcesoria - RVS : RVS 710; Akc SGE=HARMANN - Akcesoria - SGE : SGE 710; Akc SGE dla ESD=HARMANN - Akcesoria - SGE : SGE 800; B=433 mm; C=770 mm; Ciśnienie akustyczne nominalne obudowa Lpa=66 dB(A); D=710 mm; D2=716 mm; Długość MAXEE=433 mm; F=600 mm; Klasa odporności ogniowej Tmax=brak; Lookup Table Name=MAXEE; MAXEE=HARMANN - MAXEE : MAXEE 710/6/22500T; Masa=72.50 kg; Moc akustyczna nominalna obudowa Lwa=73 dB(A); Model=MAXEE 710/6/22500T; N1=15  [stored 0.0492126 ft]; Numer artykułu=15413800; Obroty nominalne nnom=11800.000 obr./min; Powietrze Przepływ Maksymalny Qmax=22569.0 m³/h; Powietrze ciśnienie statyczne maksymalne dPmax=320.0 Pa; R2=355 mm; Wysokość=303.5 mm; Wysokość FAL=119 mm; Wysokość FSD=57 mm; Zasilanie Częstotliwość Maksymalna fmax=60 Hz; Zasilanie Moc maksymalna Pmax=2210 W; Zasilanie natężenie maksymalne Imax=5 A
- MAXEE 630/6/16100T: A=720 mm; Akc ESD=HARMANN - Akcesoria - ESD : ESD 630; Akc EXP=HARMANN - Akcesoria - EXP : EXP 630; Akc FAL=HARMANN - Akcesoria - FAL : FAL 630; Akc FSD=HARMANN - Akcesoria - FSD : FSD 02; Akc RAF=HARMANN - Akcesoria - RAF : RAF 630; Akc RVK H=HARMANN - Akcesoria - RVK H : RVK H 630; Akc RVS=HARMANN - Akcesoria - RVS : RVS 630; Akc SGE=HARMANN - Akcesoria - SGE : SGE 630; Akc SGE dla ESD=HARMANN - Akcesoria - SGE : SGE 710; B=443 mm; C=690 mm; Ciśnienie akustyczne nominalne obudowa Lpa=63 dB(A); D=630 mm; D2=636 mm; Długość MAXEE=443 mm; F=486 mm; Klasa odporności ogniowej Tmax=brak; Lookup Table Name=MAXEE; MAXEE=HARMANN - MAXEE : MAXEE 630/6/16100T; Masa=52.00 kg; Moc akustyczna nominalna obudowa Lwa=70 dB(A); Model=MAXEE  630/6/16100T; N1=14  [stored 0.0459318 ft]; Numer artykułu=15415400; Obroty nominalne nnom=1260.000 obr./min; Powietrze Przepływ Maksymalny Qmax=16170.0 m³/h; Powietrze ciśnienie statyczne maksymalne dPmax=260.0 Pa; R2=315 mm; Wysokość=273.5 mm; Wysokość FAL=99 mm; Wysokość FSD=57 mm; Zasilanie Częstotliwość Maksymalna fmax=65 Hz; Zasilanie Moc maksymalna Pmax=1240 W; Zasilanie natężenie maksymalne Imax=3 A
- MAXEE 630/4/24600T: A=720 mm; Akc ESD=HARMANN - Akcesoria - ESD : ESD 630; Akc EXP=HARMANN - Akcesoria - EXP : EXP 630; Akc FAL=HARMANN - Akcesoria - FAL : FAL 630; Akc FSD=HARMANN - Akcesoria - FSD : FSD 02; Akc RAF=HARMANN - Akcesoria - RAF : RAF 630; Akc RVK H=HARMANN - Akcesoria - RVK H : RVK H 630; Akc RVS=HARMANN - Akcesoria - RVS : RVS 630; Akc SGE=HARMANN - Akcesoria - SGE : SGE 630; Akc SGE dla ESD=HARMANN - Akcesoria - SGE : SGE 710; B=443 mm; C=690 mm; Ciśnienie akustyczne nominalne obudowa Lpa=72 dB(A); D=630 mm; D2=636 mm; Długość MAXEE=443 mm; F=504 mm; Klasa odporności ogniowej Tmax=brak; Lookup Table Name=MAXEE; MAXEE=HARMANN - MAXEE : MAXEE 630/4/24600T; Masa=65.20 kg; Moc akustyczna nominalna obudowa Lwa=79 dB(A); Model=MAXEE 630/4/24600T; N1=13  [stored 0.0426509 ft]; Numer artykułu=15415200; Obroty nominalne nnom=1910.000 obr./min; Powietrze Przepływ Maksymalny Qmax=24620.0 m³/h; Powietrze ciśnienie statyczne maksymalne dPmax=625.0 Pa; R2=315 mm; Wysokość=273.5 mm; Wysokość FAL=99 mm; Wysokość FSD=57 mm; Zasilanie Częstotliwość Maksymalna fmax=65 Hz; Zasilanie Moc maksymalna Pmax=5680 W; Zasilanie natężenie maksymalne Imax=9 A
- MAXEE 560/4/16500T: A=650 mm; Akc ESD=HARMANN - Akcesoria - ESD : ESD 560; Akc EXP=HARMANN - Akcesoria - EXP : EXP 560; Akc FAL=HARMANN - Akcesoria - FAL : FAL 560; Akc FSD=HARMANN - Akcesoria - FSD : FSD 02; Akc RAF=HARMANN - Akcesoria - RAF : RAF 560; Akc RVK H=HARMANN - Akcesoria - RVK H : RVK H 560; Akc RVS=HARMANN - Akcesoria - RVS : RVS 560; Akc SGE=HARMANN - Akcesoria - SGE : SGE 560; Akc SGE dla ESD=HARMANN - Akcesoria - SGE : SGE 630; B=443 mm; C=620 mm; Ciśnienie akustyczne nominalne obudowa Lpa=67 dB(A); D=560 mm; D2=566 mm; Długość MAXEE=443 mm; F=474 mm; Klasa odporności ogniowej Tmax=brak; Lookup Table Name=MAXEE; MAXEE=HARMANN - MAXEE : MAXEE 560/4/16500T; Masa=49.30 kg; Moc akustyczna nominalna obudowa Lwa=74 dB(A); Model=MAXEE.HT 560/4/16500T; N1=12  [stored 0.0393701 ft]; Numer artykułu=15415200; Obroty nominalne nnom=1760.000 obr./min; Powietrze Przepływ Maksymalny Qmax=16580.0 m³/h; Powietrze ciśnienie statyczne maksymalne dPmax=430.0 Pa; R2=280 mm; Wysokość=238.5 mm; Wysokość FAL=99 mm; Wysokość FSD=57 mm; Zasilanie Częstotliwość Maksymalna fmax=60 Hz; Zasilanie Moc maksymalna Pmax=3160 W; Zasilanie natężenie maksymalne Imax=4 A
- MAXEE 560/4/15300T: A=650 mm; Akc ESD=HARMANN - Akcesoria - ESD : ESD 560; Akc EXP=HARMANN - Akcesoria - EXP : EXP 560; Akc FAL=HARMANN - Akcesoria - FAL : FAL 560; Akc FSD=HARMANN - Akcesoria - FSD : FSD 03; Akc RAF=HARMANN - Akcesoria - RAF : RAF 560; Akc RVK H=HARMANN - Akcesoria - RVK H : RVK H 560; Akc RVS=HARMANN - Akcesoria - RVS : RVS 560; Akc SGE=HARMANN - Akcesoria - SGE : SGE 560; Akc SGE dla ESD=HARMANN - Akcesoria - SGE : SGE 630; B=443 mm; C=620 mm; Ciśnienie akustyczne nominalne obudowa Lpa=65 dB(A); D=560 mm; D2=566 mm; Długość MAXEE=443 mm; F=515 mm; Klasa odporności ogniowej Tmax=brak; Lookup Table Name=MAXEE; MAXEE=HARMANN - MAXEE : MAXEE 560/4/15300T; Masa=42.10 kg; Moc akustyczna nominalna obudowa Lwa=72 dB(A); Model=MAXEE 560/4/15300T; N1=11  [stored 0.0360892 ft]; Numer artykułu=15415800; Obroty nominalne nnom=1610.000 obr./min; Powietrze Przepływ Maksymalny Qmax=15380.0 m³/h; Powietrze ciśnienie statyczne maksymalne dPmax=350.0 Pa; R2=280 mm; Wysokość=238.5 mm; Wysokość FAL=99 mm; Wysokość FSD=57 mm; Zasilanie Częstotliwość Maksymalna fmax=55 Hz; Zasilanie Moc maksymalna Pmax=2580 W; Zasilanie natężenie maksymalne Imax=3 A
- MAXEE 500/2/19600T: A=590 mm; Akc ESD=HARMANN - Akcesoria - ESD : ESD 500; Akc EXP=HARMANN - Akcesoria - EXP : EXP 500; Akc FAL=HARMANN - Akcesoria - FAL : FAL 500; Akc FSD=HARMANN - Akcesoria - FSD : FSD 02; Akc RAF=HARMANN - Akcesoria - RAF : RAF 500; Akc RVK H=HARMANN - Akcesoria - RVK H : RVK H 500; Akc RVS=HARMANN - Akcesoria - RVS : RVS 500; Akc SGE=HARMANN - Akcesoria - SGE : SGE 500; Akc SGE dla ESD=HARMANN - Akcesoria - SGE : SGE 560; B=443 mm; C=560 mm; Ciśnienie akustyczne nominalne obudowa Lpa=78 dB(A); D=500 mm; D2=506 mm; Długość MAXEE=443 mm; F=515 mm; Klasa odporności ogniowej Tmax=brak; Lookup Table Name=MAXEE; MAXEE=HARMANN - MAXEE : MAXEE 500/2/19600T; Masa=69.30 kg; Moc akustyczna nominalna obudowa Lwa=85 dB(A); Model=MAXEE 500/2/19600T; N1=10  [stored 0.0328084 ft]; Numer artykułu=15411800; Obroty nominalne nnom=2955.000 obr./min; Powietrze Przepływ Maksymalny Qmax=19630.0 m³/h; Powietrze ciśnienie statyczne maksymalne dPmax=970.0 Pa; R2=250 mm; Wysokość=208.5 mm; Wysokość FAL=99 mm; Wysokość FSD=57 mm; Zasilanie Częstotliwość Maksymalna fmax=50 Hz; Zasilanie Moc maksymalna Pmax=5930 W; Zasilanie natężenie maksymalne Imax=11 A
- MAXEE 500/4/11600T: A=590 mm; Akc ESD=HARMANN - Akcesoria - ESD : ESD 500; Akc EXP=HARMANN - Akcesoria - EXP : EXP 500; Akc FAL=HARMANN - Akcesoria - FAL : FAL 500; Akc FSD=HARMANN - Akcesoria - FSD : FSD 02; Akc RAF=HARMANN - Akcesoria - RAF : RAF 500; Akc RVK H=HARMANN - Akcesoria - RVK H : RVK H 500; Akc RVS=HARMANN - Akcesoria - RVS : RVS 500; Akc SGE=HARMANN - Akcesoria - SGE : SGE 500; Akc SGE dla ESD=HARMANN - Akcesoria - SGE : SGE 560; B=443 mm; C=560 mm; Ciśnienie akustyczne nominalne obudowa Lpa=64 dB(A); D=500 mm; D2=506 mm; Długość MAXEE=443 mm; F=465 mm; Klasa odporności ogniowej Tmax=brak; Lookup Table Name=MAXEE; MAXEE=HARMANN - MAXEE : MAXEE 500/4/11600T; Masa=38.50 kg; Moc akustyczna nominalna obudowa Lwa=71 dB(A); Model=MAXEE 500/4/11600T; N1=9  [stored 0.0295276 ft]; Numer artykułu=15411100; Obroty nominalne nnom=1760.000 obr./min; Powietrze Przepływ Maksymalny Qmax=11640.0 m³/h; Powietrze ciśnienie statyczne maksymalne dPmax=360.0 Pa; R2=250 mm; Wysokość=208.5 mm; Wysokość FAL=99 mm; Wysokość FSD=57 mm; Zasilanie Częstotliwość Maksymalna fmax=60 Hz; Zasilanie Moc maksymalna Pmax=1820 W; Zasilanie natężenie maksymalne Imax=3 A
- MAXEE 450/2/15300T: A=530 mm; Akc ESD=HARMANN - Akcesoria - ESD : ESD 450; Akc EXP=HARMANN - Akcesoria - EXP : EXP 450; Akc FAL=HARMANN - Akcesoria - FAL : FAL 450; Akc FSD=HARMANN - Akcesoria - FSD : FSD 01; Akc RAF=HARMANN - Akcesoria - RAF : RAF 450; Akc RVK H=HARMANN - Akcesoria - RVK H : RVK H 450; Akc RVS=HARMANN - Akcesoria - RVS : RVS 450; Akc SGE=HARMANN - Akcesoria - SGE : SGE 450; Akc SGE dla ESD=HARMANN - Akcesoria - SGE : SGE 500; B=368 mm; C=500 mm; Ciśnienie akustyczne nominalne obudowa Lpa=76 dB(A); D=450 mm; D2=456 mm; Długość MAXEE=368 mm; F=465 mm; Klasa odporności ogniowej Tmax=brak]; Lookup Table Name=MAXEE; MAXEE=HARMANN - MAXEE : MAXEE 450/2/15300T; Masa=45.60 kg; Moc akustyczna nominalna obudowa Lwa=83 dB(A); Model=MAXEE 450/2/15300T; N1=8  [stored 0.0262467 ft]; Numer artykułu=15410600; Obroty nominalne nnom=3220.000 obr./min; Powietrze Przepływ Maksymalny Qmax=15300.0 m³/h; Powietrze ciśnienie statyczne maksymalne dPmax=960.0 Pa; R2=225 mm; Wysokość=183.5 mm; Wysokość FAL=99 mm; Wysokość FSD=57 mm; Zasilanie Częstotliwość Maksymalna fmax=55 Hz; Zasilanie Moc maksymalna Pmax=6320 W; Zasilanie natężenie maksymalne Imax=8 A
- MAXEE 450/4/8400T: A=530 mm; Akc ESD=HARMANN - Akcesoria - ESD : ESD 450; Akc EXP=HARMANN - Akcesoria - EXP : EXP 450; Akc FAL=HARMANN - Akcesoria - FAL : FAL 450; Akc FSD=HARMANN - Akcesoria - FSD : FSD 02; Akc RAF=HARMANN - Akcesoria - RAF : RAF 450; Akc RVK H=HARMANN - Akcesoria - RVK H : RVK H 450; Akc RVS=HARMANN - Akcesoria - RVS : RVS 450; Akc SGE=HARMANN - Akcesoria - SGE : SGE 450; Akc SGE dla ESD=HARMANN - Akcesoria - SGE : SGE 500; B=368 mm; C=500 mm; Ciśnienie akustyczne nominalne obudowa Lpa=62 dB(A); D=450 mm; D2=456 mm; Długość MAXEE=368 mm; F=396 mm; Klasa odporności ogniowej Tmax=brak; Lookup Table Name=MAXEE; MAXEE=HARMANN - MAXEE : MAXEE 450/4/8400T; Masa=25.40 kg; Moc akustyczna nominalna obudowa Lwa=69 dB(A); Model=MAXEE 450/4/8400T; N1=7  [stored 0.0229659 ft]; Numer artykułu=15410000; Obroty nominalne nnom=1750.000 obr./min; Powietrze Przepływ Maksymalny Qmax=8460.0 m³/h; Powietrze ciśnienie statyczne maksymalne dPmax=280.0 Pa; R2=225 mm; Wysokość=183.5 mm; Wysokość FAL=99 mm; Wysokość FSD=57 mm; Zasilanie Częstotliwość Maksymalna fmax=60 Hz; Zasilanie Moc maksymalna Pmax=1130 W; Zasilanie natężenie maksymalne Imax=1 A
- MAXEE 400/2/10800T: A=480 mm; Akc ESD=HARMANN - Akcesoria - ESD : ESD 400; Akc EXP=HARMANN - Akcesoria - EXP : EXP 400; Akc FAL=HARMANN - Akcesoria - FAL : FAL 400; Akc FSD=HARMANN - Akcesoria - FSD : FSD 02; Akc RAF=HARMANN - Akcesoria - RAF : RAF 400; Akc RVK H=HARMANN - Akcesoria - RVK H : RVK H 400; Akc RVS=HARMANN - Akcesoria - RVS : RVS 400; Akc SGE=HARMANN - Akcesoria - SGE : SGE 400; Akc SGE dla ESD=HARMANN - Akcesoria - SGE : SGE 450; B=368 mm; C=450 mm; Ciśnienie akustyczne nominalne obudowa Lpa=70 dB(A); D=400 mm; D2=406 mm; Długość MAXEE=368 mm; F=396 mm; Klasa odporności ogniowej Tmax=brak; Lookup Table Name=MAXEE; MAXEE=HARMANN - MAXEE : MAXEE 400/2/10800T; Masa=29.70 kg; Moc akustyczna nominalna obudowa Lwa=77 dB(A); Model=MAXEE 400/2/10800T; N1=6  [stored 0.019685 ft]; Numer artykułu=15409600; Obroty nominalne nnom=3210.000 obr./min; Powietrze Przepływ Maksymalny Qmax=10820.0 m³/h; Powietrze ciśnienie statyczne maksymalne dPmax=750.0 Pa; R2=200 mm; Wysokość=158.5 mm; Wysokość FAL=99 mm; Wysokość FSD=57 mm; Zasilanie Częstotliwość Maksymalna fmax=55 Hz; Zasilanie Moc maksymalna Pmax=3490 W; Zasilanie natężenie maksymalne Imax=5 A
- MAXEE 400/4/6800T: A=480 mm; Akc ESD=HARMANN - Akcesoria - ESD : ESD 400; Akc EXP=HARMANN - Akcesoria - EXP : EXP 400; Akc FAL=HARMANN - Akcesoria - FAL : FAL 400; Akc FSD=HARMANN - Akcesoria - FSD : FSD 01; Akc RAF=HARMANN - Akcesoria - RAF : RAF 400; Akc RVK H=HARMANN - Akcesoria - RVK H : RVK H 400; Akc RVS=HARMANN - Akcesoria - RVS : RVS 400; Akc SGE=HARMANN - Akcesoria - SGE : SGE 400; Akc SGE dla ESD=HARMANN - Akcesoria - SGE : SGE 450; B=368 mm; C=450 mm; Ciśnienie akustyczne nominalne obudowa Lpa=62 dB(A); D=400 mm; D2=406 mm; Długość MAXEE=368 mm; F=396 mm; Klasa odporności ogniowej Tmax=400 [oC/2h]; Lookup Table Name=MAXEE; MAXEE=HARMANN - MAXEE : MAXEE 400/4/6800T; Masa=23.20 kg; Moc akustyczna nominalna obudowa Lwa=69 dB(A); Model=MAXEE 400/4/6800T; N1=5  [stored 0.0164042 ft]; Numer artykułu=15409000; Obroty nominalne nnom=20400.000 obr./min; Powietrze Przepływ Maksymalny Qmax=6890.0 m³/h; Powietrze ciśnienie statyczne maksymalne dPmax=300.0 Pa; R2=200 mm; Wysokość=158.5 mm; Wysokość FAL=99 mm; Wysokość FSD=57 mm; Zasilanie Częstotliwość Maksymalna fmax=70 Hz; Zasilanie Moc maksymalna Pmax=1010 W; Zasilanie natężenie maksymalne Imax=1 A
- MAXEE 355/2/6900T: A=420 mm; Akc ESD=HARMANN - Akcesoria - ESD : ESD 355; Akc EXP=HARMANN - Akcesoria - EXP : EXP 355; Akc FAL=HARMANN - Akcesoria - FAL : FAL 355; Akc FSD=HARMANN - Akcesoria - FSD : FSD 01; Akc RAF=HARMANN - Akcesoria - RAF : RAF 355; Akc RVK H=HARMANN - Akcesoria - RVK H : RVK H 355; Akc RVS=HARMANN - Akcesoria - RVS : RVS 355; Akc SGE=HARMANN - Akcesoria - SGE : SGE 355; Akc SGE dla ESD=HARMANN - Akcesoria - SGE : SGE 400; B=383 mm; C=395 mm; Ciśnienie akustyczne nominalne obudowa Lpa=66 dB(A); D=355 mm; D2=361 mm; Długość MAXEE=383 mm; F=396 mm; Klasa odporności ogniowej Tmax=brak; Lookup Table Name=MAXEE; MAXEE=HARMANN - MAXEE : MAXEE 355/2/6900T; Masa=21.20 kg; Moc akustyczna nominalna obudowa Lwa=73 dB(A); Model=MAXEE 355/2/6900T; N1=4  [stored 0.0131234 ft]; Numer artykułu=15412500; Obroty nominalne nnom=2910.000 obr./min; Powietrze Przepływ Maksymalny Qmax=6915.0 m³/h; Powietrze ciśnienie statyczne maksymalne dPmax=440.0 Pa; R2=177.5 mm; Wysokość=136 mm; Wysokość FAL=99 mm; Wysokość FSD=57 mm; Zasilanie Częstotliwość Maksymalna fmax=50 Hz; Zasilanie Moc maksymalna Pmax=1520 W; Zasilanie natężenie maksymalne Imax=2 A
- MAXEE 355/4/4800T: A=420 mm; Akc ESD=HARMANN - Akcesoria - ESD : ESD 355; Akc EXP=HARMANN - Akcesoria - EXP : EXP 355; Akc FAL=HARMANN - Akcesoria - FAL : FAL 355; Akc FSD=HARMANN - Akcesoria - FSD : FSD 01; Akc RAF=HARMANN - Akcesoria - RAF : RAF 355; Akc RVK H=HARMANN - Akcesoria - RVK H : RVK H 355; Akc RVS=HARMANN - Akcesoria - RVS : RVS 355; Akc SGE=HARMANN - Akcesoria - SGE : SGE 355; Akc SGE dla ESD=HARMANN - Akcesoria - SGE : SGE 400; B=383 mm; C=395 mm; Ciśnienie akustyczne nominalne obudowa Lpa=58 dB(A); D=355 mm; D2=361 mm; Długość MAXEE=383 mm; F=396 mm; Klasa odporności ogniowej Tmax=brak; Lookup Table Name=MAXEE; MAXEE=HARMANN - MAXEE : MAXEE 355/4/4800T; Masa=20.30 kg; Moc akustyczna nominalna obudowa Lwa=65 dB(A); Model=MAXEE 355/4/4800T; N1=3  [stored 0.00984252 ft]; Numer artykułu=15412300; Obroty nominalne nnom=2050.000 obr./min; Powietrze Przepływ Maksymalny Qmax=4870.0 m³/h; Powietrze ciśnienie statyczne maksymalne dPmax=230.0 Pa; R2=177.5 mm; Wysokość=136 mm; Wysokość FAL=99 mm; Wysokość FSD=57 mm; Zasilanie Częstotliwość Maksymalna fmax=70 Hz; Zasilanie Moc maksymalna Pmax=575 W; Zasilanie natężenie maksymalne Imax=1 A
- MAXEE 315/2/5800T: A=380 mm; Akc ESD=HARMANN - Akcesoria - ESD : ESD 315; Akc EXP=HARMANN - Akcesoria - EXP : EXP 315; Akc FAL=HARMANN - Akcesoria - FAL : FAL 315; Akc FSD=HARMANN - Akcesoria - FSD : FSD 01; Akc RAF=HARMANN - Akcesoria - RAF : RAF 315; Akc RVK H=HARMANN - Akcesoria - RVK H : RVK H 315; Akc RVS=HARMANN - Akcesoria - RVS : RVS 315; Akc SGE=HARMANN - Akcesoria - SGE : SGE 315; Akc SGE dla ESD=HARMANN - Akcesoria - SGE : SGE 355; B=383 mm; C=355 mm; Ciśnienie akustyczne nominalne obudowa Lpa=68 dB(A); D=315 mm; D2=321 mm; Długość MAXEE=383 mm; F=396 mm; Klasa odporności ogniowej Tmax=Brak; Lookup Table Name=MAXEE; MAXEE=HARMANN - MAXEE : MAXEE 315/2/5800T; Masa=18.50 kg; Moc akustyczna nominalna obudowa Lwa=75 dB(A); Model=MAXEE 315/2/5800T; N1=2  [stored 0.00656168 ft]; Numer artykułu=15413200; Obroty nominalne nnom=3460.000 obr./min; Powietrze Przepływ Maksymalny Qmax=5805.0 m³/h; Powietrze ciśnienie statyczne maksymalne dPmax=490.0 Pa; R2=157.5 mm; Wysokość=116.5 mm; Wysokość FAL=98 mm; Wysokość FSD=57 mm; Zasilanie Częstotliwość Maksymalna fmax=60 Hz; Zasilanie Moc maksymalna Pmax=1380 W; Zasilanie natężenie maksymalne Imax=2 A
- MAXEE 315/4/3950T: A=380 mm; Akc ESD=HARMANN - Akcesoria - ESD : ESD 315; Akc EXP=HARMANN - Akcesoria - EXP : EXP 315; Akc FAL=HARMANN - Akcesoria - FAL : FAL 315; Akc FSD=HARMANN - Akcesoria - FSD : FSD 01; Akc RAF=HARMANN - Akcesoria - RAF : RAF 315; Akc RVK H=HARMANN - Akcesoria - RVK H : RVK H 315; Akc RVS=HARMANN - Akcesoria - RVS : RVS 315; Akc SGE=HARMANN - Akcesoria - SGE : SGE 315; Akc SGE dla ESD=HARMANN - Akcesoria - SGE : SGE 355; B=383 mm; C=355 mm; Ciśnienie akustyczne nominalne obudowa Lpa=58 dB(A); D=315 mm; D2=321 mm; Długość MAXEE=383 mm; F=396 mm; Klasa odporności ogniowej Tmax=brak; Lookup Table Name=MAXEE; MAXEE=HARMANN - MAXEE : MAXEE 315/4/3900T; Masa=19.30 kg; Moc akustyczna nominalna obudowa Lwa=65 dB(A); Model=MAXEE 315/4/3950T; N1=1  [stored 0.00328084 ft]; Numer artykułu=15413400; Obroty nominalne nnom=2355.000 obr./min; Powietrze Przepływ Maksymalny Qmax=3940.0 m³/h; Powietrze ciśnienie statyczne maksymalne dPmax=215.0 Pa; R2=157.5 mm; Wysokość=116.5 mm; Wysokość FAL=98 mm; Wysokość FSD=57 mm; Zasilanie Częstotliwość Maksymalna fmax=80 Hz; Zasilanie Moc maksymalna Pmax=170 W; Zasilanie natężenie maksymalne Imax=1 A

note: [stored X ft] marks values corroborated as IEEE doubles in the binary element streams (Revit-internal decimal feet)

## geometry (parser evidence)
native form markers: Sweep x30
no freeform markers — native parametric forms only
